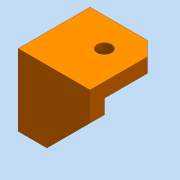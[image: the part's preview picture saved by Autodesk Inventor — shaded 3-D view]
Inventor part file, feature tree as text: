
AUTODESK INVENTOR PART (.ipt)
format: ipt  version: 2016 (Build 200138000, 138)  size: 139,776 bytes
history: native  units: mm
features: extrude x4, sketch x4, chamfer x3, hole x2
ambient origin geometry x8: Origin, YZ Plane, XZ Plane, XY Plane, X Axis, Y Axis, Z Axis, Center Point
bodies: Solid1 (feature_tree)
feature tree (13):
  extrude  "Extrusion1"  Depth=20.0mm
  extrude  "Extrusion2"  Depth=16.0mm TaperAngle=0.0deg
  hole  "Hole2"  [1 undecoded]
  hole  "Hole3"  [1 undecoded]
  chamfer  "Chamfer1"  Distance=4.0mm Angle=45.0deg
  chamfer  "Chamfer2"  Distance=7.0mm
  chamfer  "Chamfer3"  Distance=7.0mm
  sketch  "Sketch3"  dims[d15=8.0mm d16=8.0mm d17=4.0mm d18=6.0mm d19=8.0mm d20=2.0mm d21=90.0deg d22=8.0mm d23=20.594885mm]
  sketch  "Sketch4"  dims[d24=8.0mm d25=8.0mm d26=4.0mm d27=6.0mm d28=8.0mm d29=2.0mm d30=90.0deg d31=8.0mm d32=20.594885mm d42=12.0mm d43=2.0mm d44=45.0deg d45=4.0mm d46=2.0mm d47=45.0deg d48=4.0mm d49=2.0mm d50=45.0deg d51=7.0mm d52=7.0mm d53=2.0mm d54=0.0mm d55=2.0mm d56=0.0mm]
  extrude  "Extrusion3"  Depth=2.0mm TaperAngle=0.0deg
  extrude  "Extrusion4"  Depth=2.0mm TaperAngle=0.0deg
  sketch  "Sketch1"  dims[d0=20.0mm d1=20.0mm]
  sketch  "Sketch2"  dims[d2=4.0mm d3=0.0mm d4=16.0mm d5=0.0mm]
note: 2 required parameter values undecoded (feature->parameter linkage not recoverable at this tier; creation-order binding heuristic only, values carry confidence <= 0.55)
